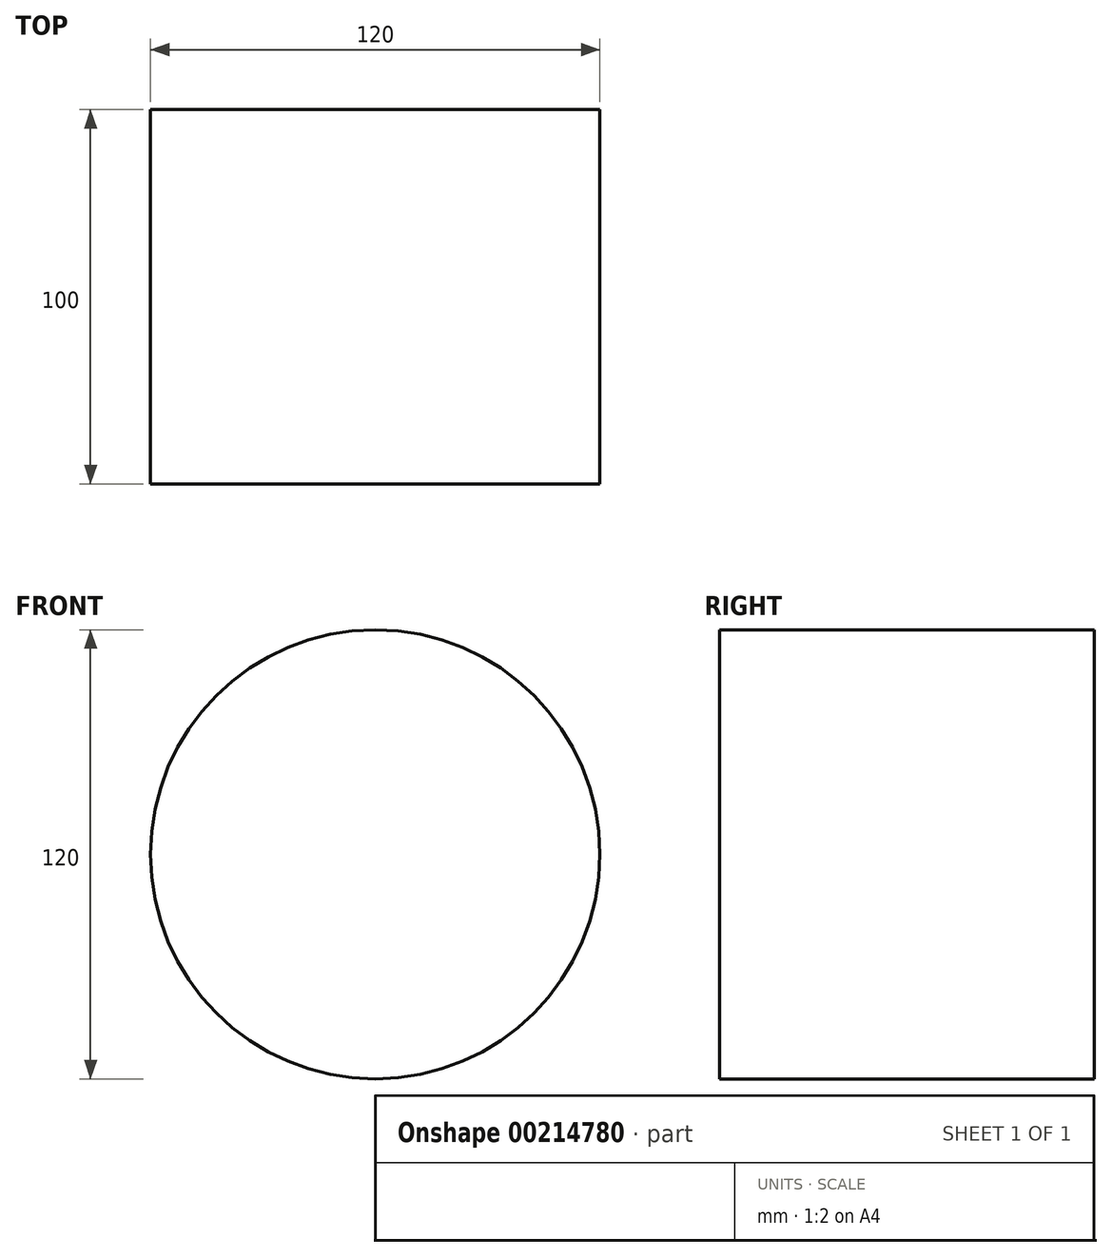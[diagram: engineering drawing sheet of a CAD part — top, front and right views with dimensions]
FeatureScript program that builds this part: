
annotation { "Feature Type Name" : "Feature", "Feature Type Description" : "" }
export const myFeature = defineFeature(function(context is Context, id is Id, definition is map)
    precondition{}
    {
        {
            var Q0;
            Q0=qCreatedBy(makeId("Front.planeOp"),FACE);
            var sketch = newSketch(context, id + "F0", { "sketchPlane" : qUnion([Q0])});
            skCircle(sketch, "E0", {"center": v(0, 0) * mm, "radius": 60 * mm});
            skSolve(sketch);
        }
        {
            var Q0;
            Q0 = qSketchRegion(id + "F0", true);
            extrude(context, id + "F1", {"entities" : qUnion([Q0]), "depth" : 100 * mm});
        }
    });
